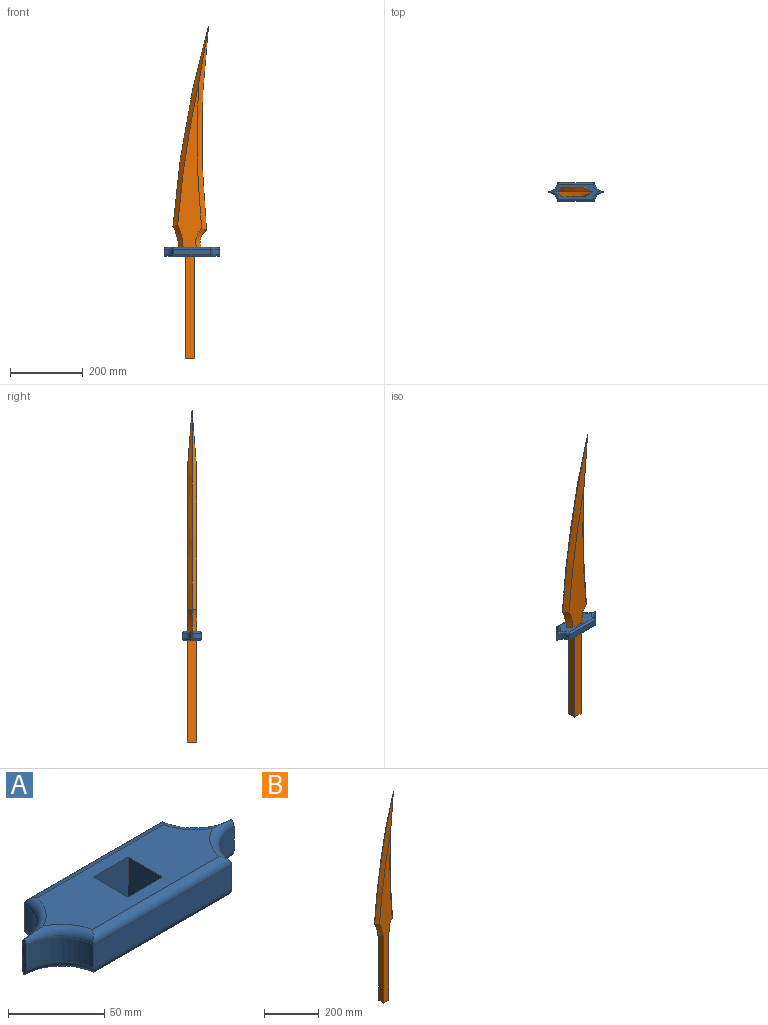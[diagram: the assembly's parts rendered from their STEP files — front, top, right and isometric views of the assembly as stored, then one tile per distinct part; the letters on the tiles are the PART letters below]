
ASSEMBLY  parts=2 mates=1
PART A: 26 faces, bbox 152.5x50.8x25.4 mm
  f0: cylinder r=25.4mm len=25.4mm, axis (0,0,-1), area 583.3mm2, adj f1,f11,f17,f23
  f1: plane 101.6x15.24mm, normal (0,1,0), area 1548.4mm2, adj f0,f2,f15,f21
  f2: cylinder r=25.4mm len=25.4mm, axis (0,0,-1), area 583.3mm2, adj f1,f3,f14,f20
  f3: plane 22.81x3.38mm, normal (-1,0,0), area 68.8mm2, adj f2,f4,f14,f16,f20,f22
  f4: cylinder r=25.4mm len=25.4mm, axis (0,0,-1), area 583.3mm2, adj f3,f5,f16,f22
  f5: plane 101.6x15.24mm, normal (0,-1,0), area 1548.4mm2, adj f4,f6,f18,f24
  f6: cylinder r=25.4mm len=25.4mm, axis (0,0,-1), area 583.3mm2, adj f5,f11,f19,f25
  f7: plane 25.4x25.4mm, normal (-1,0,0), area 645.2mm2, adj f8,f10,f12,f13
  f8: plane 25.4x25.4mm, normal (0,1,0), area 645.2mm2, adj f7,f9,f12,f13
  f9: plane 25.4x25.4mm, normal (1,0,0), area 645.2mm2, adj f8,f10,f12,f13
  f10: plane 25.4x25.4mm, normal (0,-1,0), area 645.2mm2, adj f7,f9,f12,f13
  f11: plane 22.81x3.38mm, normal (1,0,0), area 68.8mm2, adj f0,f6,f17,f19,f23,f25
  f12: plane 124.32x40.64mm, normal (0,0,1), area 3571mm2, adj f7,f8,f9,f10,f20,f21,f22,f23
  f13: plane 124.32x40.64mm, normal (0,0,-1), area 3571mm2, adj f7,f8,f9,f10,f14,f15,f16,f17
  f14: torus R=30.48mm, axis (0,0,1), area 279.5mm2, adj f2,f3,f13,f15,f16
  f15: cylinder r=5.08mm len=101.6mm, axis (-1,0,0), area 784.6mm2, adj f1,f13,f14,f17
  f16: torus R=30.48mm, axis (0,0,1), area 279.5mm2, adj f3,f4,f13,f14,f18
  f17: torus R=30.48mm, axis (0,0,1), area 279.5mm2, adj f0,f11,f13,f15,f19
  f18: cylinder r=5.08mm len=101.6mm, axis (1,0,0), area 784.6mm2, adj f5,f13,f16,f19
  f19: torus R=30.48mm, axis (0,0,1), area 279.5mm2, adj f6,f11,f13,f17,f18
  f20: torus R=30.48mm, axis (0,0,1), area 279.5mm2, adj f2,f3,f12,f21,f22
  f21: cylinder r=5.08mm len=101.6mm, axis (1,0,0), area 784.6mm2, adj f1,f12,f20,f23
  f22: torus R=30.48mm, axis (0,0,1), area 279.5mm2, adj f3,f4,f12,f20,f24
  f23: torus R=30.48mm, axis (0,0,1), area 279.5mm2, adj f0,f11,f12,f21,f25
  f24: cylinder r=5.08mm len=101.6mm, axis (-1,0,0), area 784.6mm2, adj f5,f12,f22,f25
  f25: torus R=30.48mm, axis (0,0,1), area 279.5mm2, adj f6,f11,f12,f23,f24
PART B: 15 faces, bbox 110x25.4x916 mm
  f0: plane 25.41x19.06mm, normal (0,0,-1), area 322.6mm2, adj f1,f5,f6,f7,f8
  f1: plane 304.8x25.4mm, normal (-1,0,0), area 7741.9mm2, adj f0,f2,f5,f6
  f2: plane 25.4x25.4mm, normal (0,0,-1), area 645.2mm2, adj f1,f3,f5,f6
  f3: plane 304.8x25.4mm, normal (1,0,0), area 7741.9mm2, adj f2,f4,f5,f6
  f4: plane 25.4x19.05mm, normal (0,0,-1), area 310.6mm2, adj f3,f5,f6,f13,f14
  f5: plane 752.93x66.09mm, normal (0,-1,0), area 22966.3mm2, adj f0,f1,f2,f3,f4,f8,f10,f12
  f6: plane 752.93x66.09mm, normal (0,1,0), area 22966.3mm2, adj f0,f1,f2,f3,f4,f7,f9,f11
  f7: cone r=139.7mm half-angle=45deg, axis (0,1,0), area 1113.4mm2, adj f0,f6,f8,f9
  f8: cone r=127mm half-angle=45deg, axis (0,-1,0), area 1113.4mm2, adj f0,f5,f7,f10
  f9: cone r=2844.8mm half-angle=45deg, axis (0,-1,0), area 8541.7mm2, adj f6,f7,f10,f11
  f10: cone r=2832.1mm half-angle=45deg, axis (0,1,0), area 8541.7mm2, adj f5,f8,f9,f12
  f11: cone r=2501.9mm half-angle=45deg, axis (0,1,0), area 8606.6mm2, adj f6,f9,f12,f13
  f12: cone r=2489.2mm half-angle=45deg, axis (0,-1,0), area 8606.6mm2, adj f5,f10,f11,f14
  f13: cone r=50.8mm half-angle=45deg, axis (0,1,0), area 993.9mm2, adj f4,f6,f11,f14
  f14: cone r=38.1mm half-angle=45deg, axis (0,-1,0), area 993.9mm2, adj f4,f5,f12,f13
PLACE A t=(-327.33,-203.71,-34.79)mm
PLACE B t=(-332.83,-191.01,143.01)mm
MATE fastened B.f4 <-> A.f12  axis (0,0,1) through (-314.63,-191.01,-9.39)mm
